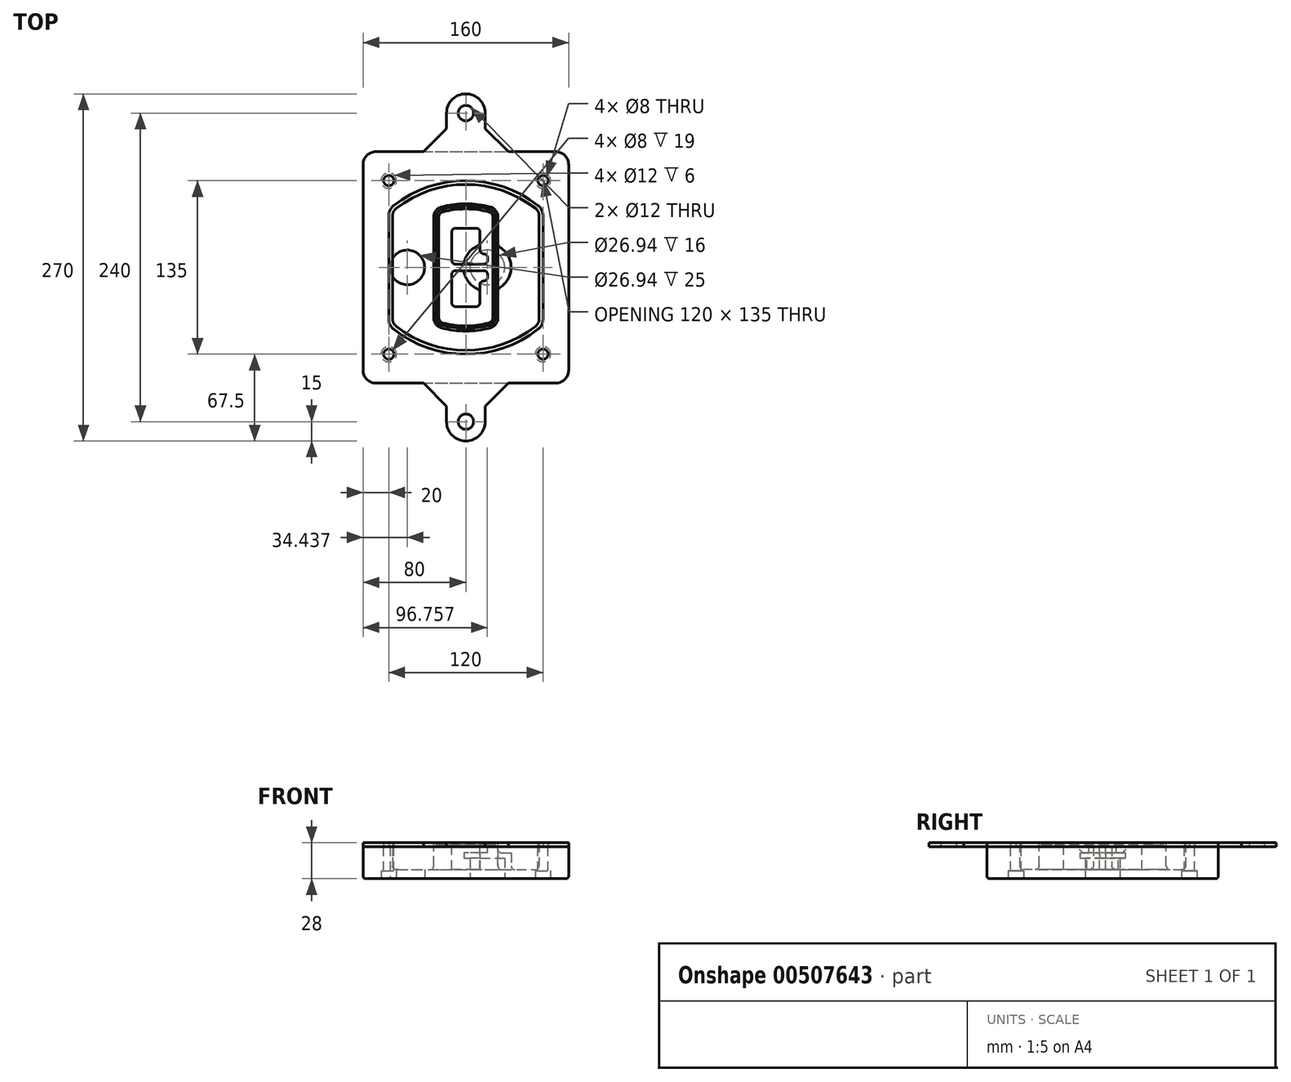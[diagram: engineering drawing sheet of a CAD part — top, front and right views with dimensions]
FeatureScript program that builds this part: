
annotation { "Feature Type Name" : "Feature", "Feature Type Description" : "" }
export const myFeature = defineFeature(function(context is Context, id is Id, definition is map)
    precondition{}
    {
        {
            var Q0;
            Q0=qCreatedBy(makeId("Top.planeOp"),FACE);
            var sketch = newSketch(context, id + "F0", { "sketchPlane" : qUnion([Q0])});
            skPoint(sketch, "E0.rect.middle", {"position": v(0, 0) * mm});
            skLineSegment(sketch, "E1.bottom", {"start": v(-70, -90) * mm, "end": v(70, -90) * mm});
            skLineSegment(sketch, "E1.top", {"start": v(-70, 90) * mm, "end": v(70, 90) * mm});
            skLineSegment(sketch, "E1.left", {"start": v(-80, -80) * mm, "end": v(-80, 80) * mm});
            skLineSegment(sketch, "E1.right", {"start": v(80, -80) * mm, "end": v(80, 80) * mm});
            skLineSegment(sketch, "E2", {"start": v(-80, 90) * mm, "end": v(80, -90) * mm, "construction": true});
            skLineSegment(sketch, "E3", {"start": v(80, 90) * mm, "end": v(-80, -90) * mm, "construction": true});
            skCircle(sketch, "E4", {"center": v(-60, 67.5) * mm, "radius": 4 * mm});
            skCircle(sketch, "E5", {"center": v(60, 67.5) * mm, "radius": 4 * mm});
            skCircle(sketch, "E6", {"center": v(60, -67.5) * mm, "radius": 4 * mm});
            skCircle(sketch, "E7", {"center": v(-60, -67.5) * mm, "radius": 4 * mm});
            skLineSegment(sketch, "E8", {"start": v(-60, 67.5) * mm, "end": v(60, 67.5) * mm, "construction": true});
            skLineSegment(sketch, "E9", {"start": v(60, 67.5) * mm, "end": v(60, -67.5) * mm, "construction": true});
            skLineSegment(sketch, "E10", {"start": v(60, -67.5) * mm, "end": v(-60, -67.5) * mm, "construction": true});
            skLineSegment(sketch, "E11", {"start": v(-60, -67.5) * mm, "end": v(-60, 67.5) * mm, "construction": true});
            skLineSegment(sketch, "E12", {"start": v(-60, 40.3) * mm, "end": v(-60, -40.3) * mm});
            skLineSegment(sketch, "E13", {"start": v(60, 40.3) * mm, "end": v(60, -40.3) * mm});
            skArc(sketch, "E14", {"start": v(56.15, 48.18) * mm, "mid": v(0, 67.5) * mm, "end": v(-56.15, 48.18) * mm});
            skArc(sketch, "E15", {"start": v(-56.15, -48.18) * mm, "mid": v(0, -67.5) * mm, "end": v(56.15, -48.18) * mm});
            skLineSegment(sketch, "E16", {"start": v(-60, 0) * mm, "end": v(60, 0) * mm, "construction": true});
            skPoint(sketch, "E17.visualSharp", {"position": v(-60, -45) * mm});
            skArc(sketch, "E17.filletArc", {"start": v(-60, -40.3) * mm, "mid": v(-58.99, -44.68) * mm, "end": v(-56.15, -48.18) * mm});
            skPoint(sketch, "E18.visualSharp", {"position": v(-60, 45) * mm});
            skArc(sketch, "E18.filletArc", {"start": v(-56.15, 48.18) * mm, "mid": v(-58.99, 44.68) * mm, "end": v(-60, 40.3) * mm});
            skPoint(sketch, "E19.visualSharp", {"position": v(60, 45) * mm});
            skArc(sketch, "E19.filletArc", {"start": v(60, 40.3) * mm, "mid": v(58.99, 44.68) * mm, "end": v(56.15, 48.18) * mm});
            skPoint(sketch, "E20.visualSharp", {"position": v(60, -45) * mm});
            skArc(sketch, "E20.filletArc", {"start": v(56.15, -48.18) * mm, "mid": v(58.99, -44.68) * mm, "end": v(60, -40.3) * mm});
            skPoint(sketch, "E21.visualSharp", {"position": v(-80, 90) * mm});
            skArc(sketch, "E21.filletArc", {"start": v(-70, 90) * mm, "mid": v(-77.07, 87.07) * mm, "end": v(-80, 80) * mm});
            skPoint(sketch, "E22.visualSharp", {"position": v(80, 90) * mm});
            skArc(sketch, "E22.filletArc", {"start": v(80, 80) * mm, "mid": v(77.07, 87.07) * mm, "end": v(70, 90) * mm});
            skPoint(sketch, "E23.visualSharp", {"position": v(80, -90) * mm});
            skArc(sketch, "E23.filletArc", {"start": v(70, -90) * mm, "mid": v(77.07, -87.07) * mm, "end": v(80, -80) * mm});
            skPoint(sketch, "E24.visualSharp", {"position": v(-80, -90) * mm});
            skArc(sketch, "E24.filletArc", {"start": v(-80, -80) * mm, "mid": v(-77.07, -87.07) * mm, "end": v(-70, -90) * mm});
            skArc(sketch, "E25.0", {"start": v(57, 40.3) * mm, "mid": v(56.3, 43.36) * mm, "end": v(54.3, 45.81) * mm});
            skLineSegment(sketch, "E25.1", {"start": v(57, 40.3) * mm, "end": v(57, -40.3) * mm});
            skArc(sketch, "E25.2", {"start": v(54.3, -45.81) * mm, "mid": v(56.3, -43.36) * mm, "end": v(57, -40.3) * mm});
            skArc(sketch, "E25.3", {"start": v(-54.3, -45.81) * mm, "mid": v(0, -64.5) * mm, "end": v(54.3, -45.81) * mm});
            skArc(sketch, "E25.4", {"start": v(-57, -40.3) * mm, "mid": v(-56.3, -43.36) * mm, "end": v(-54.3, -45.81) * mm});
            skArc(sketch, "E25.5", {"start": v(54.3, 45.81) * mm, "mid": v(0, 64.5) * mm, "end": v(-54.3, 45.81) * mm});
            skLineSegment(sketch, "E25.6", {"start": v(-57, 40.3) * mm, "end": v(-57, -40.3) * mm});
            skArc(sketch, "E25.7", {"start": v(-54.3, 45.81) * mm, "mid": v(-56.3, 43.36) * mm, "end": v(-57, 40.3) * mm});
            skArc(sketch, "E26.0", {"start": v(-58.62, 51.33) * mm, "mid": v(-62.58, 46.43) * mm, "end": v(-64, 40.3) * mm});
            skArc(sketch, "E26.1", {"start": v(58.62, 51.33) * mm, "mid": v(0, 71.5) * mm, "end": v(-58.62, 51.33) * mm});
            skArc(sketch, "E26.2", {"start": v(64, 40.3) * mm, "mid": v(62.58, 46.43) * mm, "end": v(58.62, 51.33) * mm});
            skLineSegment(sketch, "E26.3", {"start": v(64, 40.3) * mm, "end": v(64, -40.3) * mm});
            skArc(sketch, "E26.4", {"start": v(58.62, -51.33) * mm, "mid": v(62.58, -46.43) * mm, "end": v(64, -40.3) * mm});
            skLineSegment(sketch, "E26.5", {"start": v(-64, 40.3) * mm, "end": v(-64, -40.3) * mm});
            skArc(sketch, "E26.6", {"start": v(-58.62, -51.33) * mm, "mid": v(0, -71.5) * mm, "end": v(58.62, -51.33) * mm});
            skArc(sketch, "E26.7", {"start": v(-64, -40.3) * mm, "mid": v(-62.58, -46.43) * mm, "end": v(-58.62, -51.33) * mm});
            skSolve(sketch);
        }
        {
            var Q0;
            Q0=makeQuery(id+"F0.imprint","IMPRINT",FACE,{"disambiguationData":[TD([[makeQuery(id+"F0.imprint","IMPRINT",EDGE,{"derivedFrom":sQuery(id+"F0.wireOp",EDGE,"E1.bottom")}),1.0]])]});
            var Q1;
            Q1=makeQuery(id+"F0.imprint","IMPRINT",FACE,{"disambiguationData":[TD([[makeQuery(id+"F0.imprint","IMPRINT",EDGE,{"derivedFrom":sQuery(id+"F0.wireOp",EDGE,"E12")}),1.0]])]});
            var Q2;
            Q2=makeQuery(id+"F0.imprint","IMPRINT",FACE,{"disambiguationData":[TD([[makeQuery(id+"F0.imprint","IMPRINT",EDGE,{"derivedFrom":sQuery(id+"F0.wireOp",EDGE,"E25.0")}),1.0]])]});
            var Q3;
            Q3=makeQuery(id+"F0.imprint","IMPRINT",FACE,{"disambiguationData":[TD([[makeQuery(id+"F0.imprint","IMPRINT",EDGE,{"derivedFrom":sQuery(id+"F0.wireOp",EDGE,"E12")}),-1.0]])]});
            extrude(context, id + "F1", {"entities" : qUnion([Q0, Q1, Q2, Q3]), "oppositeDirection" : true, "depth" : 25 * mm});
        }
        {
            var Q0;
            Q0=makeQuery(id+"F0.imprint","IMPRINT",FACE,{"disambiguationData":[TD([[makeQuery(id+"F0.imprint","IMPRINT",EDGE,{"derivedFrom":sQuery(id+"F0.wireOp",EDGE,"E12")}),1.0]])]});
            extrude(context, id + "F2", {"entities" : qUnion([Q0]), "operationType" : NewBodyOperationType.ADD, "depth" : 3 * mm});
        }
        {
            var Q0;
            Q0=makeQuery(id+"F0.imprint","IMPRINT",FACE,{"disambiguationData":[TD([[makeQuery(id+"F0.imprint","IMPRINT",EDGE,{"derivedFrom":sQuery(id+"F0.wireOp",EDGE,"E25.0")}),1.0]])]});
            extrude(context, id + "F3", {"entities" : qUnion([Q0]), "operationType" : NewBodyOperationType.REMOVE, "oppositeDirection" : true, "depth" : 18 * mm});
        }
        {
            var Q0;
            Q0=makeQuery(id+"F2.opExtrude","CAP_FACE",FACE,{"disambiguationData":[OSD([sQuery(id+"F0.wireOp",EDGE,"E12"),sQuery(id+"F0.wireOp",EDGE,"E13"),sQuery(id+"F0.wireOp",EDGE,"E14"),sQuery(id+"F0.wireOp",EDGE,"E15"),sQuery(id+"F0.wireOp",EDGE,"E17.filletArc"),sQuery(id+"F0.wireOp",EDGE,"E18.filletArc"),sQuery(id+"F0.wireOp",EDGE,"E19.filletArc"),sQuery(id+"F0.wireOp",EDGE,"E20.filletArc"),sQuery(id+"F0.wireOp",EDGE,"E25.0"),sQuery(id+"F0.wireOp",EDGE,"E25.1"),sQuery(id+"F0.wireOp",EDGE,"E25.2"),sQuery(id+"F0.wireOp",EDGE,"E25.3"),sQuery(id+"F0.wireOp",EDGE,"E25.4"),sQuery(id+"F0.wireOp",EDGE,"E25.5"),sQuery(id+"F0.wireOp",EDGE,"E25.6"),sQuery(id+"F0.wireOp",EDGE,"E25.7")])],"isStart":false});
            var sketch = newSketch(context, id + "F4", { "sketchPlane" : qUnion([Q0])});
            skArc(sketch, "E27.0", {"start": v(-19.08, -46.97) * mm, "mid": v(0, -49.5) * mm, "end": v(19.08, -46.97) * mm});
            skArc(sketch, "E28.0", {"start": v(19.08, 46.97) * mm, "mid": v(0, 49.5) * mm, "end": v(-19.08, 46.97) * mm});
            skLineSegment(sketch, "E29", {"start": v(-25, 39.25) * mm, "end": v(-25, -39.25) * mm});
            skLineSegment(sketch, "E30", {"start": v(25, 39.25) * mm, "end": v(25, -39.25) * mm});
            skLineSegment(sketch, "E31", {"start": v(-25, 45.1) * mm, "end": v(25, 45.1) * mm, "construction": true});
            skLineSegment(sketch, "E32", {"start": v(-25, -45.1) * mm, "end": v(25, -45.1) * mm, "construction": true});
            skPoint(sketch, "E33.visualSharp", {"position": v(-25, 45.1) * mm});
            skArc(sketch, "E33.filletArc", {"start": v(-19.08, 46.97) * mm, "mid": v(-23.35, 44.11) * mm, "end": v(-25, 39.25) * mm});
            skPoint(sketch, "E34.visualSharp", {"position": v(25, 45.1) * mm});
            skArc(sketch, "E34.filletArc", {"start": v(25, 39.25) * mm, "mid": v(23.35, 44.11) * mm, "end": v(19.08, 46.97) * mm});
            skPoint(sketch, "E35.visualSharp", {"position": v(25, -45.1) * mm});
            skArc(sketch, "E35.filletArc", {"start": v(19.08, -46.97) * mm, "mid": v(23.35, -44.11) * mm, "end": v(25, -39.25) * mm});
            skPoint(sketch, "E36.visualSharp", {"position": v(-25, -45.1) * mm});
            skArc(sketch, "E36.filletArc", {"start": v(-25, -39.25) * mm, "mid": v(-23.35, -44.11) * mm, "end": v(-19.08, -46.97) * mm});
            skArc(sketch, "E37.0", {"start": v(54.3, 45.81) * mm, "mid": v(0, 64.5) * mm, "end": v(-54.3, 45.81) * mm});
            skArc(sketch, "E37.1", {"start": v(-54.3, 45.81) * mm, "mid": v(-56.3, 43.36) * mm, "end": v(-57, 40.3) * mm});
            skLineSegment(sketch, "E37.2", {"start": v(-57, 40.3) * mm, "end": v(-57, -40.3) * mm});
            skArc(sketch, "E37.3", {"start": v(-57, -40.3) * mm, "mid": v(-56.3, -43.36) * mm, "end": v(-54.3, -45.81) * mm});
            skArc(sketch, "E37.4", {"start": v(-54.3, -45.81) * mm, "mid": v(0, -64.5) * mm, "end": v(54.3, -45.81) * mm});
            skArc(sketch, "E37.5", {"start": v(54.3, -45.81) * mm, "mid": v(56.3, -43.36) * mm, "end": v(57, -40.3) * mm});
            skLineSegment(sketch, "E37.6", {"start": v(57, 40.3) * mm, "end": v(57, -40.3) * mm});
            skArc(sketch, "E37.7", {"start": v(57, 40.3) * mm, "mid": v(56.3, 43.36) * mm, "end": v(54.3, 45.81) * mm});
            skLineSegment(sketch, "E38.0", {"start": v(23, 39.25) * mm, "end": v(23, -39.25) * mm});
            skArc(sketch, "E38.1", {"start": v(18.56, -45.04) * mm, "mid": v(21.76, -42.9) * mm, "end": v(23, -39.25) * mm});
            skArc(sketch, "E38.2", {"start": v(-18.56, -45.04) * mm, "mid": v(0, -47.5) * mm, "end": v(18.56, -45.04) * mm});
            skArc(sketch, "E38.3", {"start": v(-23, -39.25) * mm, "mid": v(-21.76, -42.9) * mm, "end": v(-18.56, -45.04) * mm});
            skLineSegment(sketch, "E38.4", {"start": v(-23, 39.25) * mm, "end": v(-23, -39.25) * mm});
            skArc(sketch, "E38.5", {"start": v(23, 39.25) * mm, "mid": v(21.76, 42.9) * mm, "end": v(18.56, 45.04) * mm});
            skArc(sketch, "E38.6", {"start": v(-18.56, 45.04) * mm, "mid": v(-21.76, 42.9) * mm, "end": v(-23, 39.25) * mm});
            skArc(sketch, "E38.7", {"start": v(18.56, 45.04) * mm, "mid": v(0, 47.5) * mm, "end": v(-18.56, 45.04) * mm});
            skArc(sketch, "E39.0", {"start": v(21, 39.25) * mm, "mid": v(20.18, 41.68) * mm, "end": v(18.04, 43.1) * mm});
            skLineSegment(sketch, "E39.1", {"start": v(21, 39.25) * mm, "end": v(21, -39.25) * mm});
            skArc(sketch, "E39.2", {"start": v(18.04, -43.1) * mm, "mid": v(20.18, -41.68) * mm, "end": v(21, -39.25) * mm});
            skArc(sketch, "E39.3", {"start": v(-18.04, -43.1) * mm, "mid": v(0, -45.5) * mm, "end": v(18.04, -43.1) * mm});
            skArc(sketch, "E39.4", {"start": v(-21, -39.25) * mm, "mid": v(-20.18, -41.68) * mm, "end": v(-18.04, -43.1) * mm});
            skArc(sketch, "E39.5", {"start": v(18.04, 43.1) * mm, "mid": v(0, 45.5) * mm, "end": v(-18.04, 43.1) * mm});
            skLineSegment(sketch, "E39.6", {"start": v(-21, 39.25) * mm, "end": v(-21, -39.25) * mm});
            skArc(sketch, "E39.7", {"start": v(-18.04, 43.1) * mm, "mid": v(-20.18, 41.68) * mm, "end": v(-21, 39.25) * mm});
            skLineSegment(sketch, "E40", {"start": v(-25, 0) * mm, "end": v(25, 0) * mm, "construction": true});
            skLineSegment(sketch, "E41", {"start": v(-11, 5.5) * mm, "end": v(-11, 27.5) * mm});
            skLineSegment(sketch, "E42", {"start": v(-8, 30.5) * mm, "end": v(8, 30.5) * mm});
            skLineSegment(sketch, "E43", {"start": v(11, 27.5) * mm, "end": v(11, 13.5) * mm});
            skLineSegment(sketch, "E44", {"start": v(14, 10.5) * mm, "end": v(14, 10.5) * mm});
            skLineSegment(sketch, "E45", {"start": v(17, 7.5) * mm, "end": v(17, 5.5) * mm});
            skLineSegment(sketch, "E46", {"start": v(14, 2.5) * mm, "end": v(-8, 2.5) * mm});
            skPoint(sketch, "E47.visualSharp", {"position": v(-11, 30.5) * mm});
            skArc(sketch, "E47.filletArc", {"start": v(-8, 30.5) * mm, "mid": v(-10.12, 29.62) * mm, "end": v(-11, 27.5) * mm});
            skPoint(sketch, "E48.visualSharp", {"position": v(11, 30.5) * mm});
            skArc(sketch, "E48.filletArc", {"start": v(11, 27.5) * mm, "mid": v(10.12, 29.62) * mm, "end": v(8, 30.5) * mm});
            skPoint(sketch, "E49.visualSharp", {"position": v(11, 10.5) * mm});
            skArc(sketch, "E49.filletArc", {"start": v(11, 13.5) * mm, "mid": v(11.88, 11.38) * mm, "end": v(14, 10.5) * mm});
            skPoint(sketch, "E50.visualSharp", {"position": v(17, 10.5) * mm});
            skArc(sketch, "E50.filletArc", {"start": v(17, 7.5) * mm, "mid": v(16.12, 9.62) * mm, "end": v(14, 10.5) * mm});
            skPoint(sketch, "E51.visualSharp", {"position": v(17, 2.5) * mm});
            skArc(sketch, "E51.filletArc", {"start": v(14, 2.5) * mm, "mid": v(16.12, 3.38) * mm, "end": v(17, 5.5) * mm});
            skPoint(sketch, "E52.visualSharp", {"position": v(-11, 2.5) * mm});
            skArc(sketch, "E52.filletArc", {"start": v(-11, 5.5) * mm, "mid": v(-10.12, 3.38) * mm, "end": v(-8, 2.5) * mm});
            skLineSegment(sketch, "E53.0.MirrorCS", {"start": v(14, -2.5) * mm, "end": v(-8, -2.5) * mm});
            skArc(sketch, "E54.0.MirrorCS", {"start": v(-11, -5.5) * mm, "mid": v(-10.12, -3.38) * mm, "end": v(-8, -2.5) * mm});
            skLineSegment(sketch, "E55.0.MirrorCS", {"start": v(-11, -5.5) * mm, "end": v(-11, -27.5) * mm});
            skArc(sketch, "E56.0.MirrorCS", {"start": v(-8, -30.5) * mm, "mid": v(-10.12, -29.62) * mm, "end": v(-11, -27.5) * mm});
            skLineSegment(sketch, "E57.0.MirrorCS", {"start": v(-8, -30.5) * mm, "end": v(8, -30.5) * mm});
            skArc(sketch, "E58.0.MirrorCS", {"start": v(11, -27.5) * mm, "mid": v(10.12, -29.62) * mm, "end": v(8, -30.5) * mm});
            skLineSegment(sketch, "E59.0.MirrorCS", {"start": v(11, -27.5) * mm, "end": v(11, -13.5) * mm});
            skArc(sketch, "E60.0.MirrorCS", {"start": v(11, -13.5) * mm, "mid": v(11.88, -11.38) * mm, "end": v(14, -10.5) * mm});
            skArc(sketch, "E61.0.MirrorCS", {"start": v(17, -7.5) * mm, "mid": v(16.12, -9.62) * mm, "end": v(14, -10.5) * mm});
            skLineSegment(sketch, "E62.0.MirrorCS", {"start": v(17, -7.5) * mm, "end": v(17, -5.5) * mm});
            skArc(sketch, "E63.0.MirrorCS", {"start": v(14, -2.5) * mm, "mid": v(16.12, -3.38) * mm, "end": v(17, -5.5) * mm});
            skSolve(sketch);
        }
        {
            var Q0;
            Q0=makeQuery(id+"F4.imprint","IMPRINT",FACE,{"disambiguationData":[TD([[makeQuery(id+"F4.imprint","IMPRINT",EDGE,{"derivedFrom":sQuery(id+"F4.wireOp",EDGE,"E27.0")}),1.0]])]});
            var Q1;
            Q1=makeQuery(id+"F4.imprint","IMPRINT",FACE,{"disambiguationData":[TD([[makeQuery(id+"F4.imprint","IMPRINT",EDGE,{"derivedFrom":sQuery(id+"F4.wireOp",EDGE,"E38.0")}),-1.0]])]});
            var Q2;
            Q2=makeQuery(id+"F4.imprint","IMPRINT",FACE,{"disambiguationData":[TD([[makeQuery(id+"F4.imprint","IMPRINT",EDGE,{"derivedFrom":sQuery(id+"F4.wireOp",EDGE,"E39.0")}),1.0]])]});
            extrude(context, id + "F5", {"entities" : qUnion([Q0, Q1, Q2]), "operationType" : NewBodyOperationType.ADD, "endBound" : BoundingType.UP_TO_NEXT, "oppositeDirection" : true, "depth" : 25 * mm});
        }
        {
            var Q0;
            Q0=makeQuery(id+"F4.imprint","IMPRINT",FACE,{"disambiguationData":[TD([[makeQuery(id+"F4.imprint","IMPRINT",EDGE,{"derivedFrom":sQuery(id+"F4.wireOp",EDGE,"E38.0")}),-1.0]])]});
            extrude(context, id + "F6", {"entities" : qUnion([Q0]), "operationType" : NewBodyOperationType.REMOVE, "oppositeDirection" : true, "depth" : 2 * mm});
        }
        {
            var Q0;
            Q0=makeQuery(id+"F1.opExtrude","CAP_FACE",FACE,{"disambiguationData":[OSD([sQuery(id+"F0.wireOp",EDGE,"E1.bottom"),sQuery(id+"F0.wireOp",EDGE,"E1.top"),sQuery(id+"F0.wireOp",EDGE,"E1.left"),sQuery(id+"F0.wireOp",EDGE,"E1.right"),sQuery(id+"F0.wireOp",EDGE,"E4"),sQuery(id+"F0.wireOp",EDGE,"E5"),sQuery(id+"F0.wireOp",EDGE,"E6"),sQuery(id+"F0.wireOp",EDGE,"E7"),sQuery(id+"F0.wireOp",EDGE,"E21.filletArc"),sQuery(id+"F0.wireOp",EDGE,"E22.filletArc"),sQuery(id+"F0.wireOp",EDGE,"E23.filletArc"),sQuery(id+"F0.wireOp",EDGE,"E24.filletArc")])],"isStart":false});
            var sketch = newSketch(context, id + "F7", { "sketchPlane" : qUnion([Q0])});
            skCircle(sketch, "E64", {"center": v(16.76, 0) * mm, "radius": 13.47 * mm});
            skCircle(sketch, "E65", {"center": v(-45.56, 0) * mm, "radius": 13.47 * mm});
            skLineSegment(sketch, "E66", {"start": v(80, 0) * mm, "end": v(-80, 0) * mm});
            skCircle(sketch, "E67", {"center": v(16.76, 0) * mm, "radius": 18.47 * mm});
            skCircle(sketch, "E68", {"center": v(60, -67.5) * mm, "radius": 6 * mm});
            skCircle(sketch, "E69", {"center": v(-60, -67.5) * mm, "radius": 6 * mm});
            skCircle(sketch, "E70", {"center": v(-60, 67.5) * mm, "radius": 6 * mm});
            skCircle(sketch, "E71", {"center": v(60, 67.5) * mm, "radius": 6 * mm});
            skSolve(sketch);
        }
        {
            var Q0;
            {var subQ1=sQuery(id+"F7.wireOp",EDGE,"E66");var subQ4=sQuery(id+"F7.wireOp",EDGE,"E64");var subQ6=makeQuery(id+"F7.imprint","INTERSECT",VERTEX,{"disambiguationData":[OD(0.0)],"derivedFrom":[subQ4,subQ1]});Q0=makeQuery(id+"F7.imprint","IMPRINT",FACE,{"disambiguationData":[TD([[makeQuery(id+"F7.imprint","IMPRINT",EDGE,{"disambiguationData":[TD([[subQ6,-1.0]])],"derivedFrom":subQ4}),-1.0]])]});}
            var Q1;
            {var subQ0=sQuery(id+"F7.wireOp",EDGE,"E66");var subQ1=sQuery(id+"F7.wireOp",EDGE,"E64");var subQ3=makeQuery(id+"F7.imprint","INTERSECT",VERTEX,{"disambiguationData":[OD(0.0)],"derivedFrom":[subQ1,subQ0]});Q1=makeQuery(id+"F7.imprint","IMPRINT",FACE,{"disambiguationData":[TD([[makeQuery(id+"F7.imprint","IMPRINT",EDGE,{"disambiguationData":[TD([[subQ3,-1.0]])],"derivedFrom":subQ1}),1.0]])]});}
            var Q2;
            {var subQ0=sQuery(id+"F7.wireOp",EDGE,"E66");var subQ1=sQuery(id+"F7.wireOp",EDGE,"E64");var subQ3=makeQuery(id+"F7.imprint","INTERSECT",VERTEX,{"disambiguationData":[OD(0.0)],"derivedFrom":[subQ1,subQ0]});Q2=makeQuery(id+"F7.imprint","IMPRINT",FACE,{"disambiguationData":[TD([[makeQuery(id+"F7.imprint","IMPRINT",EDGE,{"disambiguationData":[TD([[subQ3,1.0]])],"derivedFrom":subQ1}),1.0]])]});}
            var Q3;
            {var subQ1=sQuery(id+"F7.wireOp",EDGE,"E66");var subQ4=sQuery(id+"F7.wireOp",EDGE,"E64");var subQ6=makeQuery(id+"F7.imprint","INTERSECT",VERTEX,{"disambiguationData":[OD(0.0)],"derivedFrom":[subQ4,subQ1]});Q3=makeQuery(id+"F7.imprint","IMPRINT",FACE,{"disambiguationData":[TD([[makeQuery(id+"F7.imprint","IMPRINT",EDGE,{"disambiguationData":[TD([[subQ6,1.0]])],"derivedFrom":subQ4}),-1.0]])]});}
            extrude(context, id + "F8", {"entities" : qUnion([Q0, Q1, Q2, Q3]), "operationType" : NewBodyOperationType.ADD, "oppositeDirection" : true, "depth" : 20 * mm});
        }
        {
            var Q0;
            {var subQ0=sQuery(id+"F7.wireOp",EDGE,"E66");var subQ1=sQuery(id+"F7.wireOp",EDGE,"E64");var subQ3=makeQuery(id+"F7.imprint","INTERSECT",VERTEX,{"disambiguationData":[OD(0.0)],"derivedFrom":[subQ1,subQ0]});Q0=makeQuery(id+"F7.imprint","IMPRINT",FACE,{"disambiguationData":[TD([[makeQuery(id+"F7.imprint","IMPRINT",EDGE,{"disambiguationData":[TD([[subQ3,-1.0]])],"derivedFrom":subQ1}),1.0]])]});}
            var Q1;
            {var subQ0=sQuery(id+"F7.wireOp",EDGE,"E66");var subQ1=sQuery(id+"F7.wireOp",EDGE,"E64");var subQ3=makeQuery(id+"F7.imprint","INTERSECT",VERTEX,{"disambiguationData":[OD(0.0)],"derivedFrom":[subQ1,subQ0]});Q1=makeQuery(id+"F7.imprint","IMPRINT",FACE,{"disambiguationData":[TD([[makeQuery(id+"F7.imprint","IMPRINT",EDGE,{"disambiguationData":[TD([[subQ3,1.0]])],"derivedFrom":subQ1}),1.0]])]});}
            extrude(context, id + "F9", {"entities" : qUnion([Q0, Q1]), "operationType" : NewBodyOperationType.REMOVE, "oppositeDirection" : true, "depth" : 16 * mm});
        }
        {
            var Q0;
            {var subQ0=sQuery(id+"F7.wireOp",EDGE,"E66");var subQ1=sQuery(id+"F7.wireOp",EDGE,"E65");var subQ3=makeQuery(id+"F7.imprint","INTERSECT",VERTEX,{"disambiguationData":[OD(0.0)],"derivedFrom":[subQ1,subQ0]});Q0=makeQuery(id+"F7.imprint","IMPRINT",FACE,{"disambiguationData":[TD([[makeQuery(id+"F7.imprint","IMPRINT",EDGE,{"disambiguationData":[TD([[subQ3,-1.0]])],"derivedFrom":subQ1}),1.0]])]});}
            var Q1;
            {var subQ0=sQuery(id+"F7.wireOp",EDGE,"E66");var subQ1=sQuery(id+"F7.wireOp",EDGE,"E65");var subQ3=makeQuery(id+"F7.imprint","INTERSECT",VERTEX,{"disambiguationData":[OD(0.0)],"derivedFrom":[subQ1,subQ0]});Q1=makeQuery(id+"F7.imprint","IMPRINT",FACE,{"disambiguationData":[TD([[makeQuery(id+"F7.imprint","IMPRINT",EDGE,{"disambiguationData":[TD([[subQ3,1.0]])],"derivedFrom":subQ1}),1.0]])]});}
            extrude(context, id + "F10", {"entities" : qUnion([Q0, Q1]), "operationType" : NewBodyOperationType.REMOVE, "oppositeDirection" : true, "depth" : 25 * mm});
        }
        {
            var Q0;
            Q0=makeQuery(id+"F7.imprint","IMPRINT",FACE,{"disambiguationData":[TD([[makeQuery(id+"F7.imprint","IMPRINT",EDGE,{"derivedFrom":sQuery(id+"F7.wireOp",EDGE,"E68")}),1.0]])]});
            var Q1;
            Q1=makeQuery(id+"F7.imprint","IMPRINT",FACE,{"disambiguationData":[TD([[makeQuery(id+"F7.imprint","IMPRINT",EDGE,{"derivedFrom":makeQuery(id+"F1.opExtrude","CAP_EDGE",EDGE,{"disambiguationData":[OSD([sQuery(id+"F0.wireOp",EDGE,"E5")])],"isStart":false})}),-1.0]])]});
            var Q2;
            Q2=makeQuery(id+"F7.imprint","IMPRINT",FACE,{"disambiguationData":[TD([[makeQuery(id+"F7.imprint","IMPRINT",EDGE,{"derivedFrom":sQuery(id+"F7.wireOp",EDGE,"E69")}),1.0]])]});
            var Q3;
            Q3=makeQuery(id+"F7.imprint","IMPRINT",FACE,{"disambiguationData":[TD([[makeQuery(id+"F7.imprint","IMPRINT",EDGE,{"derivedFrom":makeQuery(id+"F1.opExtrude","CAP_EDGE",EDGE,{"disambiguationData":[OSD([sQuery(id+"F0.wireOp",EDGE,"E4")])],"isStart":false})}),-1.0]])]});
            var Q4;
            Q4=makeQuery(id+"F7.imprint","IMPRINT",FACE,{"disambiguationData":[TD([[makeQuery(id+"F7.imprint","IMPRINT",EDGE,{"derivedFrom":sQuery(id+"F7.wireOp",EDGE,"E70")}),1.0]])]});
            var Q5;
            Q5=makeQuery(id+"F7.imprint","IMPRINT",FACE,{"disambiguationData":[TD([[makeQuery(id+"F7.imprint","IMPRINT",EDGE,{"derivedFrom":makeQuery(id+"F1.opExtrude","CAP_EDGE",EDGE,{"disambiguationData":[OSD([sQuery(id+"F0.wireOp",EDGE,"E7")])],"isStart":false})}),-1.0]])]});
            var Q6;
            Q6=makeQuery(id+"F7.imprint","IMPRINT",FACE,{"disambiguationData":[TD([[makeQuery(id+"F7.imprint","IMPRINT",EDGE,{"derivedFrom":sQuery(id+"F7.wireOp",EDGE,"E71")}),1.0]])]});
            var Q7;
            Q7=makeQuery(id+"F7.imprint","IMPRINT",FACE,{"disambiguationData":[TD([[makeQuery(id+"F7.imprint","IMPRINT",EDGE,{"derivedFrom":makeQuery(id+"F1.opExtrude","CAP_EDGE",EDGE,{"disambiguationData":[OSD([sQuery(id+"F0.wireOp",EDGE,"E6")])],"isStart":false})}),-1.0]])]});
            extrude(context, id + "F11", {"entities" : qUnion([Q0, Q1, Q2, Q3, Q4, Q5, Q6, Q7]), "operationType" : NewBodyOperationType.REMOVE, "oppositeDirection" : true, "depth" : 6 * mm});
        }
        {
            var Q0;
            Q0=makeQuery(id+"F9.boolean.opBoolean","COPY",FACE,{"derivedFrom":makeQuery(id+"F9.opExtrude","CAP_FACE",FACE,{"disambiguationData":[OSD([sQuery(id+"F7.wireOp",EDGE,"E64")])],"isStart":false})});
            var sketch = newSketch(context, id + "F12", { "sketchPlane" : qUnion([Q0])});
            skArc(sketch, "E72.0", {"start": v(11, 17.55) * mm, "mid": v(2.57, 11.82) * mm, "end": v(-1.54, 2.5) * mm});
            skArc(sketch, "E72.1", {"start": v(-1.54, -2.5) * mm, "mid": v(2.57, -11.82) * mm, "end": v(11, -17.55) * mm});
            skLineSegment(sketch, "E73", {"start": v(-1.54, -2.5) * mm, "end": v(14, -2.5) * mm});
            skLineSegment(sketch, "E74.0", {"start": v(14, 2.5) * mm, "end": v(-1.54, 2.5) * mm});
            skArc(sketch, "E74.1", {"start": v(14, 2.5) * mm, "mid": v(16.12, 3.38) * mm, "end": v(17, 5.5) * mm});
            skLineSegment(sketch, "E74.2", {"start": v(17, 7.5) * mm, "end": v(17, 5.5) * mm});
            skArc(sketch, "E74.3", {"start": v(17, 7.5) * mm, "mid": v(16.12, 9.62) * mm, "end": v(14, 10.5) * mm});
            skArc(sketch, "E74.4", {"start": v(11, 13.5) * mm, "mid": v(11.88, 11.38) * mm, "end": v(14, 10.5) * mm});
            skLineSegment(sketch, "E74.5", {"start": v(11, 17.55) * mm, "end": v(11, 13.5) * mm});
            skLineSegment(sketch, "E74.7", {"start": v(14, -2.5) * mm, "end": v(-1.54, -2.5) * mm});
            skArc(sketch, "E74.8", {"start": v(14, -2.5) * mm, "mid": v(16.12, -3.38) * mm, "end": v(17, -5.5) * mm});
            skLineSegment(sketch, "E74.9", {"start": v(17, -7.5) * mm, "end": v(17, -5.5) * mm});
            skArc(sketch, "E74.10", {"start": v(17, -7.5) * mm, "mid": v(16.12, -9.62) * mm, "end": v(14, -10.5) * mm});
            skArc(sketch, "E74.11", {"start": v(11, -13.5) * mm, "mid": v(11.88, -11.38) * mm, "end": v(14, -10.5) * mm});
            skLineSegment(sketch, "E74.12", {"start": v(11, -17.55) * mm, "end": v(11, -13.5) * mm});
            skPoint(sketch, "E75.orphan", {"position": v(11, -27.5) * mm});
            skPoint(sketch, "E76.orphan", {"position": v(-8, -2.5) * mm});
            skPoint(sketch, "E77.orphan", {"position": v(-8, 2.5) * mm});
            skPoint(sketch, "E78.orphan", {"position": v(11, 27.5) * mm});
            skSolve(sketch);
        }
        {
            var Q0;
            {var subQ7=sQuery(id+"F12.wireOp",EDGE,"E72.0");var subQ14=sQuery(id+"F12.wireOp",EDGE,"E72.1");var subQ16=sQuery(id+"F12.wireOp",EDGE,"E74.1");var subQ18=sQuery(id+"F12.wireOp",EDGE,"E74.8");Q0=qUnion([makeQuery(id+"F12.imprint","IMPRINT",FACE,{"disambiguationData":[TD([[makeQuery(id+"F12.imprint","IMPRINT",EDGE,{"derivedFrom":subQ7}),1.0]])]}),makeQuery(id+"F12.imprint","IMPRINT",FACE,{"disambiguationData":[TD([[makeQuery(id+"F12.imprint","IMPRINT",EDGE,{"derivedFrom":subQ14}),1.0]])]}),makeQuery(id+"F12.imprint","IMPRINT",FACE,{"disambiguationData":[TD([[makeQuery(id+"F12.imprint","IMPRINT",EDGE,{"derivedFrom":subQ16}),1.0]])]}),makeQuery(id+"F12.imprint","IMPRINT",FACE,{"disambiguationData":[TD([[makeQuery(id+"F12.imprint","IMPRINT",EDGE,{"derivedFrom":subQ18}),-1.0]])]})]);}
            var Q1;
            Q1=makeQuery(id+"F5.boolean.opBoolean","SPLIT",FACE,{"disambiguationData":[TD([makeQuery(id+"F5.opExtrude","SWEPT_FACE",FACE,{"disambiguationData":[OSD([sQuery(id+"F4.wireOp",EDGE,"E41")])]})])],"derivedFrom":makeQuery(id+"F3.boolean.opBoolean","COPY",FACE,{"derivedFrom":makeQuery(id+"F3.opExtrude","CAP_FACE",FACE,{"disambiguationData":[OSD([sQuery(id+"F0.wireOp",EDGE,"E25.0"),sQuery(id+"F0.wireOp",EDGE,"E25.1"),sQuery(id+"F0.wireOp",EDGE,"E25.2"),sQuery(id+"F0.wireOp",EDGE,"E25.3"),sQuery(id+"F0.wireOp",EDGE,"E25.4"),sQuery(id+"F0.wireOp",EDGE,"E25.5"),sQuery(id+"F0.wireOp",EDGE,"E25.6"),sQuery(id+"F0.wireOp",EDGE,"E25.7")])],"isStart":false})})});
            extrude(context, id + "F13", {"entities" : qUnion([Q0]), "operationType" : NewBodyOperationType.REMOVE, "endBound" : BoundingType.UP_TO_SURFACE, "endBoundEntityFace" : qUnion([Q1]), "depth" : 25 * mm});
        }
        {
            var Q0;
            Q0=makeQuery(id+"F3.boolean.opBoolean","COPY",EDGE,{"derivedFrom":makeQuery(id+"F3.opExtrude","CAP_EDGE",EDGE,{"disambiguationData":[OSD([sQuery(id+"F0.wireOp",EDGE,"E25.6")])],"isStart":false})});
            var Q1;
            Q1=makeQuery(id+"F8.boolean.opBoolean","INTERSECT",EDGE,{"derivedFrom":[makeQuery(id+"F5.opExtrude","SWEPT_FACE",FACE,{"disambiguationData":[OSD([sQuery(id+"F4.wireOp",EDGE,"E30")])]}),makeQuery(id+"F8.opExtrude","CAP_FACE",FACE,{"disambiguationData":[OSD([sQuery(id+"F7.wireOp",EDGE,"E67")])],"isStart":false})]});
            var Q2;
            Q2=makeQuery(id+"F8.boolean.opBoolean","INTERSECT",EDGE,{"disambiguationData":[OD(1.0)],"derivedFrom":[makeQuery(id+"F5.opExtrude","SWEPT_FACE",FACE,{"disambiguationData":[OSD([sQuery(id+"F4.wireOp",EDGE,"E30")])]}),makeQuery(id+"F8.opExtrude","SWEPT_FACE",FACE,{"disambiguationData":[OSD([sQuery(id+"F7.wireOp",EDGE,"E67")])]})]});
            var Q3;
            {var subQ0=sQuery(id+"F4.wireOp",EDGE,"E30");Q3=makeQuery(id+"F8.boolean.opBoolean","SPLIT",EDGE,{"disambiguationData":[TD([makeQuery(id+"F5.opExtrude","SWEPT_FACE",FACE,{"disambiguationData":[OSD([sQuery(id+"F4.wireOp",EDGE,"E35.filletArc")])]})])],"derivedFrom":makeQuery(id+"F5.opExtrude","CAP_EDGE",EDGE,{"disambiguationData":[OSD([subQ0])],"isStart":false})});}
            var Q4;
            {var subQ0=sQuery(id+"F0.wireOp",EDGE,"E25.7");var subQ1=sQuery(id+"F0.wireOp",EDGE,"E25.1");var subQ2=sQuery(id+"F0.wireOp",EDGE,"E25.6");var subQ3=sQuery(id+"F0.wireOp",EDGE,"E25.5");var subQ4=sQuery(id+"F0.wireOp",EDGE,"E25.4");var subQ5=sQuery(id+"F0.wireOp",EDGE,"E25.0");var subQ6=sQuery(id+"F0.wireOp",EDGE,"E25.2");var subQ7=sQuery(id+"F0.wireOp",EDGE,"E25.3");Q4=makeQuery(id+"F8.boolean.opBoolean","INTERSECT",EDGE,{"derivedFrom":[makeQuery(id+"F5.boolean.opBoolean","SPLIT",FACE,{"disambiguationData":[TD([makeQuery(id+"F2.opExtrude","SWEPT_FACE",FACE,{"disambiguationData":[OSD([subQ5])]})])],"derivedFrom":makeQuery(id+"F3.boolean.opBoolean","COPY",FACE,{"derivedFrom":makeQuery(id+"F3.opExtrude","CAP_FACE",FACE,{"disambiguationData":[OSD([subQ5,subQ1,subQ6,subQ7,subQ4,subQ3,subQ2,subQ0])],"isStart":false})})}),makeQuery(id+"F8.opExtrude","SWEPT_FACE",FACE,{"disambiguationData":[OSD([sQuery(id+"F7.wireOp",EDGE,"E67")])]})]});}
            var Q5;
            Q5=makeQuery(id+"F8.boolean.opBoolean","INTERSECT",EDGE,{"disambiguationData":[OD(0.0)],"derivedFrom":[makeQuery(id+"F5.opExtrude","SWEPT_FACE",FACE,{"disambiguationData":[OSD([sQuery(id+"F4.wireOp",EDGE,"E30")])]}),makeQuery(id+"F8.opExtrude","SWEPT_FACE",FACE,{"disambiguationData":[OSD([sQuery(id+"F7.wireOp",EDGE,"E67")])]})]});
            fillet(context, id + "F14", {"entities" : qUnion([Q0, Q1, Q2, Q3, Q4, Q5]), "radius" : 3 * mm, "tangentPropagation" : true, "allowEdgeOverflow" : false});
        }
        {
            var Q0;
            Q0=makeQuery(id+"F1.opExtrude","CAP_EDGE",EDGE,{"disambiguationData":[OSD([sQuery(id+"F0.wireOp",EDGE,"E1.bottom")])],"isStart":false});
            fillet(context, id + "F15", {"entities" : qUnion([Q0]), "radius" : 2 * mm, "tangentPropagation" : true, "allowEdgeOverflow" : false});
        }
        {
            var Q0;
            Q0=qCreatedBy(makeId("Top.planeOp"),FACE);
            var sketch = newSketch(context, id + "F16", { "sketchPlane" : qUnion([Q0])});
            skLineSegment(sketch, "E79.0", {"start": v(-70, 90) * mm, "end": v(70, 90) * mm});
            skArc(sketch, "E79.1", {"start": v(80, 80) * mm, "mid": v(77.07, 87.07) * mm, "end": v(70, 90) * mm});
            skArc(sketch, "E79.2", {"start": v(-70, 90) * mm, "mid": v(-77.07, 87.07) * mm, "end": v(-80, 80) * mm});
            skLineSegment(sketch, "E79.3", {"start": v(-80, -80) * mm, "end": v(-80, 80) * mm});
            skLineSegment(sketch, "E79.4", {"start": v(80, -80) * mm, "end": v(80, 80) * mm});
            skArc(sketch, "E79.5", {"start": v(70, -90) * mm, "mid": v(77.07, -87.07) * mm, "end": v(80, -80) * mm});
            skLineSegment(sketch, "E79.6", {"start": v(-70, -90) * mm, "end": v(70, -90) * mm});
            skArc(sketch, "E79.7", {"start": v(-80, -80) * mm, "mid": v(-77.07, -87.07) * mm, "end": v(-70, -90) * mm});
            skCircle(sketch, "E79.8", {"center": v(-60, 67.5) * mm, "radius": 4 * mm});
            skCircle(sketch, "E79.9", {"center": v(60, 67.5) * mm, "radius": 4 * mm});
            skCircle(sketch, "E79.10", {"center": v(60, -67.5) * mm, "radius": 4 * mm});
            skCircle(sketch, "E79.11", {"center": v(-60, -67.5) * mm, "radius": 4 * mm});
            skArc(sketch, "E79.12", {"start": v(-56.15, -48.18) * mm, "mid": v(0, -67.5) * mm, "end": v(56.15, -48.18) * mm});
            skArc(sketch, "E79.13", {"start": v(-60, -40.3) * mm, "mid": v(-58.99, -44.68) * mm, "end": v(-56.15, -48.18) * mm});
            skLineSegment(sketch, "E79.14", {"start": v(-60, 40.3) * mm, "end": v(-60, -40.3) * mm});
            skArc(sketch, "E79.15", {"start": v(-56.15, 48.18) * mm, "mid": v(-58.99, 44.68) * mm, "end": v(-60, 40.3) * mm});
            skArc(sketch, "E79.16", {"start": v(56.15, 48.18) * mm, "mid": v(0, 67.5) * mm, "end": v(-56.15, 48.18) * mm});
            skArc(sketch, "E79.17", {"start": v(60, 40.3) * mm, "mid": v(58.99, 44.68) * mm, "end": v(56.15, 48.18) * mm});
            skLineSegment(sketch, "E79.18", {"start": v(60, 40.3) * mm, "end": v(60, -40.3) * mm});
            skArc(sketch, "E79.19", {"start": v(56.15, -48.18) * mm, "mid": v(58.99, -44.68) * mm, "end": v(60, -40.3) * mm});
            skLineSegment(sketch, "E80", {"start": v(0, 90) * mm, "end": v(0, 120) * mm, "construction": true});
            skCircle(sketch, "E81", {"center": v(0, 120) * mm, "radius": 6 * mm});
            skLineSegment(sketch, "E82", {"start": v(-33, 90) * mm, "end": v(-15, 108) * mm});
            skLineSegment(sketch, "E83", {"start": v(-15, 108) * mm, "end": v(-15, 120) * mm});
            skLineSegment(sketch, "E84", {"start": v(33, 90) * mm, "end": v(15, 108) * mm});
            skLineSegment(sketch, "E85", {"start": v(15, 108) * mm, "end": v(15, 120) * mm});
            skArc(sketch, "E86", {"start": v(15, 120) * mm, "mid": v(0, 135) * mm, "end": v(-15, 120) * mm});
            skLineSegment(sketch, "E87", {"start": v(-80, 0) * mm, "end": v(80, 0) * mm, "construction": true});
            skArc(sketch, "E88.MirrorCS", {"start": v(-15, 120) * mm, "mid": v(0, 135) * mm, "end": v(15, 120) * mm});
            skLineSegment(sketch, "E89.MirrorCS", {"start": v(80, 0) * mm, "end": v(-80, 0) * mm, "construction": true});
            skLineSegment(sketch, "E90.MirrorCS", {"start": v(33, -90) * mm, "end": v(15, -108) * mm});
            skArc(sketch, "E91.MirrorCS", {"start": v(15, -120) * mm, "mid": v(0, -135) * mm, "end": v(-15, -120) * mm});
            skLineSegment(sketch, "E92.MirrorCS", {"start": v(-15, -108) * mm, "end": v(-15, -120) * mm});
            skLineSegment(sketch, "E93.MirrorCS", {"start": v(-33, -90) * mm, "end": v(-15, -108) * mm});
            skLineSegment(sketch, "E94.MirrorCS", {"start": v(15, -108) * mm, "end": v(15, -120) * mm});
            skCircle(sketch, "E95.MirrorC", {"center": v(0, -120) * mm, "radius": 6 * mm});
            skLineSegment(sketch, "E96.MirrorCS", {"start": v(0, -90) * mm, "end": v(0, -120) * mm, "construction": true});
            skSolve(sketch);
        }
        {
            var Q0;
            Q0 = qSketchRegion(id + "F16", true);
            var Q1;
            Q1=makeQuery(id+"F2.opExtrude","CAP_FACE",FACE,{"disambiguationData":[OSD([sQuery(id+"F0.wireOp",EDGE,"E12"),sQuery(id+"F0.wireOp",EDGE,"E13"),sQuery(id+"F0.wireOp",EDGE,"E14"),sQuery(id+"F0.wireOp",EDGE,"E15"),sQuery(id+"F0.wireOp",EDGE,"E17.filletArc"),sQuery(id+"F0.wireOp",EDGE,"E18.filletArc"),sQuery(id+"F0.wireOp",EDGE,"E19.filletArc"),sQuery(id+"F0.wireOp",EDGE,"E20.filletArc"),sQuery(id+"F0.wireOp",EDGE,"E25.0"),sQuery(id+"F0.wireOp",EDGE,"E25.1"),sQuery(id+"F0.wireOp",EDGE,"E25.2"),sQuery(id+"F0.wireOp",EDGE,"E25.3"),sQuery(id+"F0.wireOp",EDGE,"E25.4"),sQuery(id+"F0.wireOp",EDGE,"E25.5"),sQuery(id+"F0.wireOp",EDGE,"E25.6"),sQuery(id+"F0.wireOp",EDGE,"E25.7")])],"isStart":false});
            extrude(context, id + "F17", {"entities" : qUnion([Q0]), "endBound" : BoundingType.UP_TO_SURFACE, "endBoundEntityFace" : qUnion([Q1]), "depth" : 25 * mm});
        }
    });
